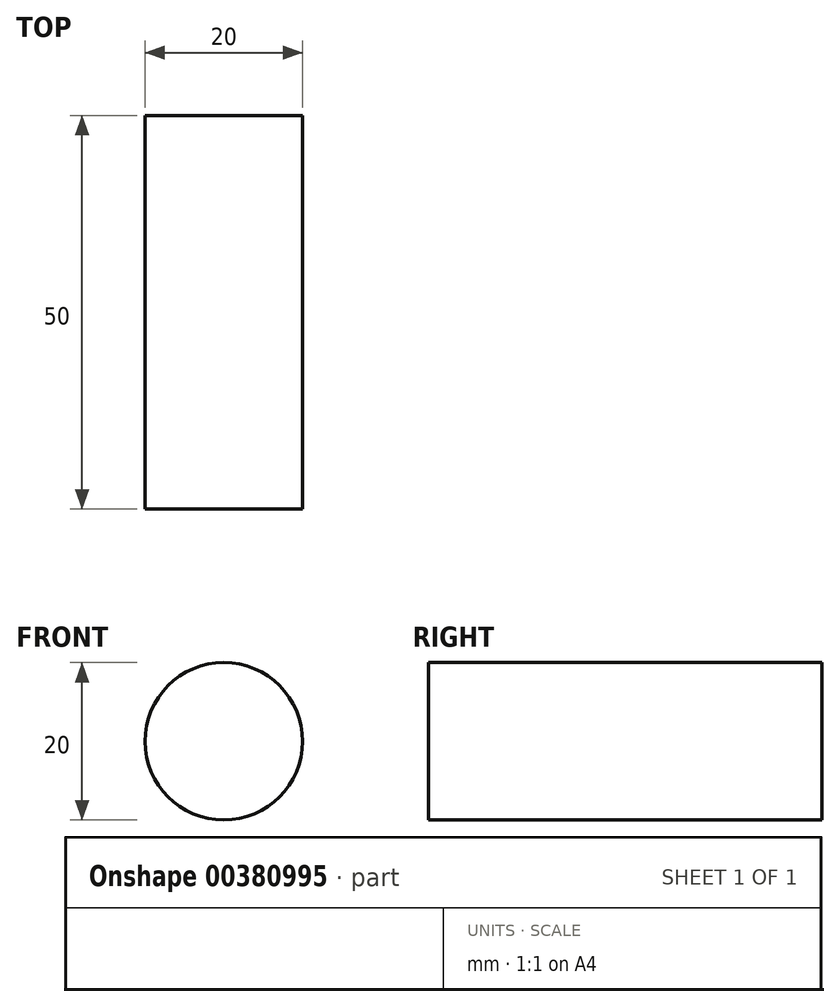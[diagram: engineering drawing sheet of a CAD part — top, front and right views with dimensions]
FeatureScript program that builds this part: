
annotation { "Feature Type Name" : "Feature", "Feature Type Description" : "" }
export const myFeature = defineFeature(function(context is Context, id is Id, definition is map)
    precondition{}
    {
        {
            var Q0;
            Q0=qCreatedBy(makeId("Front.planeOp"),FACE);
            var sketch = newSketch(context, id + "F0", { "sketchPlane" : qUnion([Q0])});
            skCircle(sketch, "E0", {"center": v(0, 0) * mm, "radius": 10 * mm});
            skSolve(sketch);
        }
        {
            var Q0;
            Q0 = qSketchRegion(id + "F0", true);
            extrude(context, id + "F1", {"entities" : qUnion([Q0]), "endBound" : BoundingType.SYMMETRIC, "depth" : 50 * mm});
        }
    });
